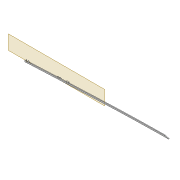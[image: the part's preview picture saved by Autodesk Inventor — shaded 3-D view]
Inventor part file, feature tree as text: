
AUTODESK INVENTOR PART (.ipt)
format: ipt  version: 2022 (Build 260153000, 153)  size: 587,264 bytes
history: native  units: mm
features: projected_geometry x11, sketch x9, extrude x8, shell x1, fillet x1, plane x1, chamfer x1
ambient origin geometry x8: Origin, YZ Plane, XZ Plane, XY Plane, X Axis, Y Axis, Z Axis, Center Point
bodies: Solid1 (feature_tree)
feature tree (32):
  extrude  "Extrusion1"  Depth=4.0mm
  shell  "Shell1"  Thickness=2.0mm
  extrude  "Extrusion8"  Depth=5.9mm
  extrude  "Extrusion3"  Depth=10.0mm TaperAngle=0.0deg
  extrude  "Extrusion4"  Depth=5.0mm
  fillet  "Fillet1"  Radius=5.0mm
  sketch  "Sketch10"  dims[d22=2.0mm d23=0.0mm d31=2.0mm d32=5.0mm]
  extrude  "Extrusion5"  Depth=2.5mm
  plane  "Work Plane2"
  extrude  "Extrusion9"  Depth=5.0mm
  extrude  "Extrusion10"  Depth=80.0mm
  chamfer  "Chamfer1"  Distance=2.0mm
  extrude  "Extrusion12"  Depth=5.0mm
  sketch  "Sketch29"  dims[d63=6.0mm d64=2.0mm d65=0.0mm]
  sketch  "Sketch30"  dims[d66=3.0mm d67=12.0mm d68=5.0mm d69=10.0mm d70=12.0mm d71=3.05mm d72=10.0mm d73=0.0mm d75=100.0mm d76=20.0mm d78=10.0mm d79=0.0mm d82=3.0mm d83=2.0mm d84=45.0deg d85=1.0mm d86=1.0mm d87=1.0mm d88=1.0mm d89=1.0mm d90=1.0mm d91=10.0mm d92=0.0mm d93=0.5mm]
  sketch  "Sketch3"  dims[d0=2.0mm d1=0.0mm d2=4.0mm d7=2.0mm]
  sketch  "Sketch8"  dims[d8=2.0mm d9=5.9mm]
  sketch  "Sketch9"  dims[d13=10.0mm d14=0.0mm d16=10.0mm d17=0.0mm]
  projected_geometry  "Projected Loop4"
  projected_geometry  "Projected Loop10"
  sketch  "Sketch24"  dims[d34=1.6mm d35=2.5mm]
  projected_geometry  "Projected Loop11"
  projected_geometry  "Projected Loop12"
  projected_geometry  "Projected Loop13"
  sketch  "Sketch26"  dims[d37=5.0mm d38=1.6mm]
  projected_geometry  "Projected Loop14"
  sketch  "Sketch28"  dims[d40=2.5mm d62=80.0mm]
  projected_geometry  "Project Cut Edges1"
  projected_geometry  "Project Cut Edges2"
  projected_geometry  "Project Cut Edges3"
  projected_geometry  "Project Cut Edges4"
  projected_geometry  "Project Cut Edges5"
